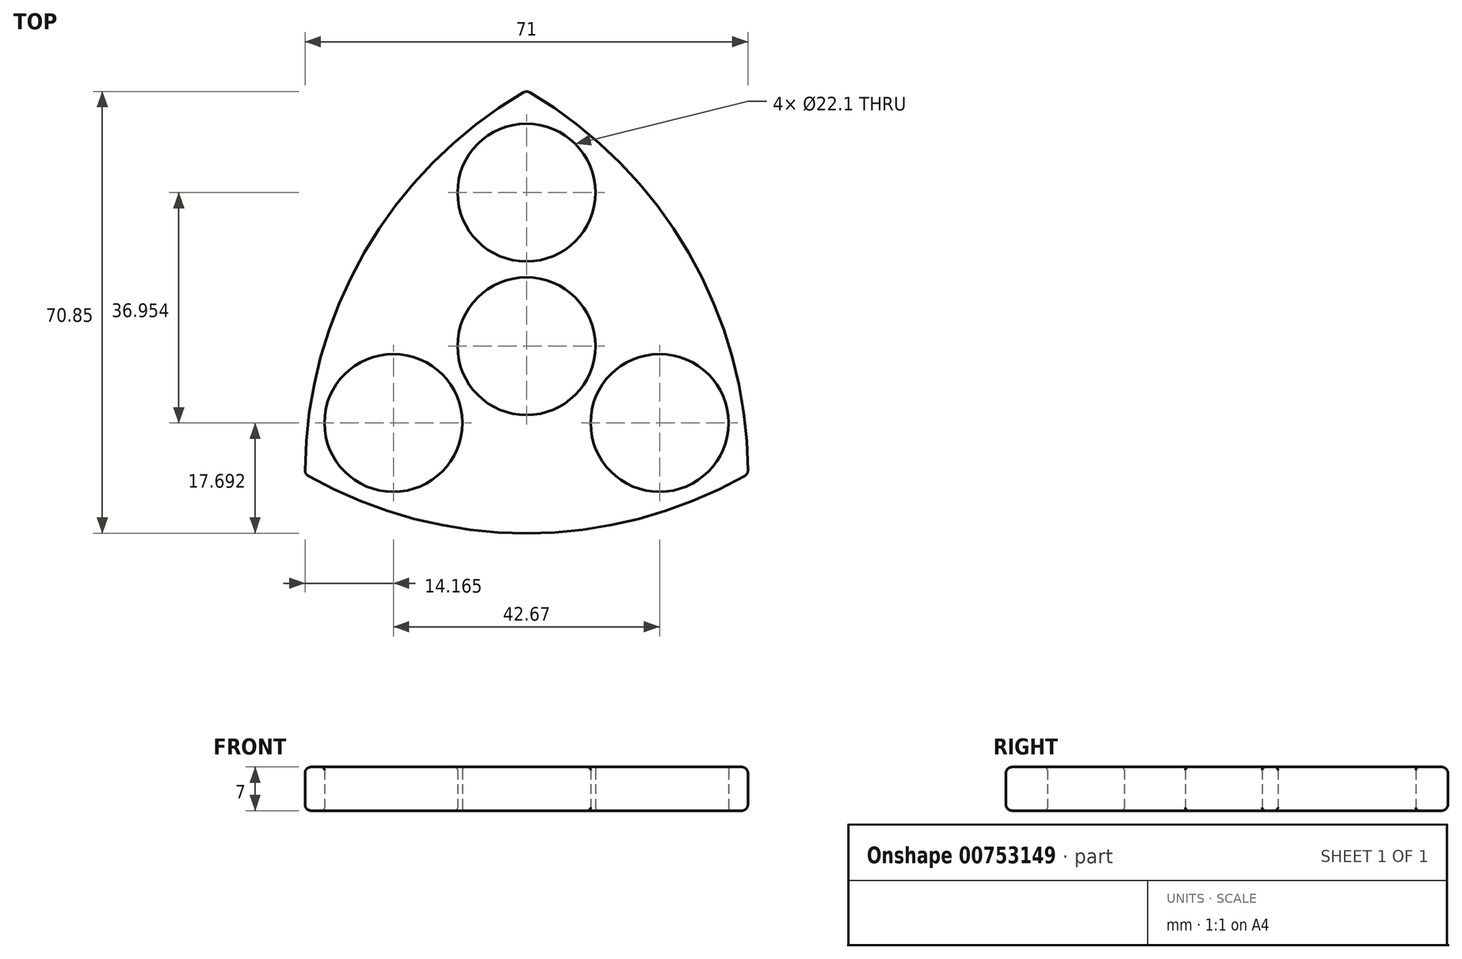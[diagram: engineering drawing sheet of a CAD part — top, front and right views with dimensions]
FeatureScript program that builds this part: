
annotation { "Feature Type Name" : "Feature", "Feature Type Description" : "" }
export const myFeature = defineFeature(function(context is Context, id is Id, definition is map)
    precondition{}
    {
        {
            var Q0;
            Q0=qCreatedBy(makeId("Top.planeOp"),FACE);
            var sketch = newSketch(context, id + "F0", { "sketchPlane" : qUnion([Q0])});
            skCircle(sketch, "E0", {"center": v(0, 0) * mm, "radius": 11.05 * mm});
            skCircle(sketch, "E1.cCircle", {"center": v(0, 0) * mm, "radius": 41 * mm, "construction": true});
            skLineSegment(sketch, "E1.0", {"start": v(35.5, -20.5) * mm, "end": v(-35.5, -20.5) * mm, "construction": true});
            skLineSegment(sketch, "E1.1", {"start": v(-35.5, -20.5) * mm, "end": v(0, 41) * mm, "construction": true});
            skLineSegment(sketch, "E1.2", {"start": v(0, 41) * mm, "end": v(35.5, -20.5) * mm, "construction": true});
            skArc(sketch, "E2", {"start": v(35.5, -20.5) * mm, "mid": v(26, 15) * mm, "end": v(0, 41) * mm});
            skArc(sketch, "E3", {"start": v(0, 41) * mm, "mid": v(-26, 15) * mm, "end": v(-35.5, -20.5) * mm});
            skArc(sketch, "E4", {"start": v(-35.5, -20.5) * mm, "mid": v(0, -30.01) * mm, "end": v(35.5, -20.5) * mm});
            skLineSegment(sketch, "E5", {"start": v(35.5, -20.5) * mm, "end": v(0, 0) * mm, "construction": true});
            skLineSegment(sketch, "E6", {"start": v(0, 41) * mm, "end": v(0, 0) * mm, "construction": true});
            skLineSegment(sketch, "E7", {"start": v(-35.5, -20.5) * mm, "end": v(0, 0) * mm, "construction": true});
            skCircle(sketch, "E8", {"center": v(-21.34, -12.32) * mm, "radius": 11.05 * mm});
            skCircle(sketch, "E9.1.0", {"center": v(21.34, -12.32) * mm, "radius": 11.05 * mm});
            skCircle(sketch, "E9.2.0", {"center": v(0, 24.64) * mm, "radius": 11.05 * mm});
            skSolve(sketch);
        }
        {
            var Q0;
            Q0 = qSketchRegion(id + "F0", true);
            extrude(context, id + "F1", {"entities" : qUnion([Q0]), "depth" : 7 * mm, "offsetDistance" : 25 * mm});
        }
        {
            var Q0;
            Q0=makeQuery(id+"F1.opExtrude","CAP_EDGE",EDGE,{"disambiguationData":[OSD([sQuery(id+"F0.wireOp",EDGE,"E4")])],"isStart":false});
            var Q1;
            Q1=makeQuery(id+"F1.opExtrude","CAP_EDGE",EDGE,{"disambiguationData":[OSD([sQuery(id+"F0.wireOp",EDGE,"E2")])],"isStart":false});
            var Q2;
            Q2=makeQuery(id+"F1.opExtrude","CAP_EDGE",EDGE,{"disambiguationData":[OSD([sQuery(id+"F0.wireOp",EDGE,"E3")])],"isStart":false});
            var Q3;
            Q3=makeQuery(id+"F1.opExtrude","CAP_EDGE",EDGE,{"disambiguationData":[OSD([sQuery(id+"F0.wireOp",EDGE,"E2")])],"isStart":true});
            var Q4;
            Q4=makeQuery(id+"F1.opExtrude","CAP_EDGE",EDGE,{"disambiguationData":[OSD([sQuery(id+"F0.wireOp",EDGE,"E4")])],"isStart":true});
            var Q5;
            Q5=makeQuery(id+"F1.opExtrude","CAP_EDGE",EDGE,{"disambiguationData":[OSD([sQuery(id+"F0.wireOp",EDGE,"E3")])],"isStart":true});
            var Q6;
            Q6=makeQuery(id+"F1.opExtrude","SWEPT_EDGE",EDGE,{"disambiguationData":[OSD([sQuery(id+"F0.wireOp",EDGE,"E3"),sQuery(id+"F0.wireOp",EDGE,"E4")])]});
            var Q7;
            Q7=makeQuery(id+"F1.opExtrude","SWEPT_EDGE",EDGE,{"disambiguationData":[OSD([sQuery(id+"F0.wireOp",EDGE,"E2"),sQuery(id+"F0.wireOp",EDGE,"E3")])]});
            var Q8;
            Q8=makeQuery(id+"F1.opExtrude","SWEPT_EDGE",EDGE,{"disambiguationData":[OSD([sQuery(id+"F0.wireOp",EDGE,"E2"),sQuery(id+"F0.wireOp",EDGE,"E4")])]});
            fillet(context, id + "F2", {"entities" : qUnion([Q0, Q1, Q2, Q3, Q4, Q5, Q6, Q7, Q8]), "radius" : 1 * mm, "tangentPropagation" : true, "allowEdgeOverflow" : false});
        }
        {
            var Q0;
            Q0=makeQuery(id+"F1.opExtrude","CAP_EDGE",EDGE,{"disambiguationData":[OSD([sQuery(id+"F0.wireOp",EDGE,"E8")])],"isStart":false});
            var Q1;
            Q1=makeQuery(id+"F1.opExtrude","CAP_EDGE",EDGE,{"disambiguationData":[OSD([sQuery(id+"F0.wireOp",EDGE,"E0")])],"isStart":false});
            var Q2;
            Q2=makeQuery(id+"F1.opExtrude","CAP_EDGE",EDGE,{"disambiguationData":[OSD([sQuery(id+"F0.wireOp",EDGE,"E9.2.0")])],"isStart":false});
            var Q3;
            Q3=makeQuery(id+"F1.opExtrude","CAP_EDGE",EDGE,{"disambiguationData":[OSD([sQuery(id+"F0.wireOp",EDGE,"E9.1.0")])],"isStart":false});
            var Q4;
            Q4=makeQuery(id+"F1.opExtrude","CAP_EDGE",EDGE,{"disambiguationData":[OSD([sQuery(id+"F0.wireOp",EDGE,"E9.1.0")])],"isStart":true});
            var Q5;
            Q5=makeQuery(id+"F1.opExtrude","CAP_EDGE",EDGE,{"disambiguationData":[OSD([sQuery(id+"F0.wireOp",EDGE,"E0")])],"isStart":true});
            var Q6;
            Q6=makeQuery(id+"F1.opExtrude","CAP_EDGE",EDGE,{"disambiguationData":[OSD([sQuery(id+"F0.wireOp",EDGE,"E8")])],"isStart":true});
            var Q7;
            Q7=makeQuery(id+"F1.opExtrude","CAP_EDGE",EDGE,{"disambiguationData":[OSD([sQuery(id+"F0.wireOp",EDGE,"E9.2.0")])],"isStart":true});
            fillet(context, id + "F3", {"entities" : qUnion([Q0, Q1, Q2, Q3, Q4, Q5, Q6, Q7]), "radius" : 0.5 * mm, "tangentPropagation" : true, "allowEdgeOverflow" : false});
        }
    });
